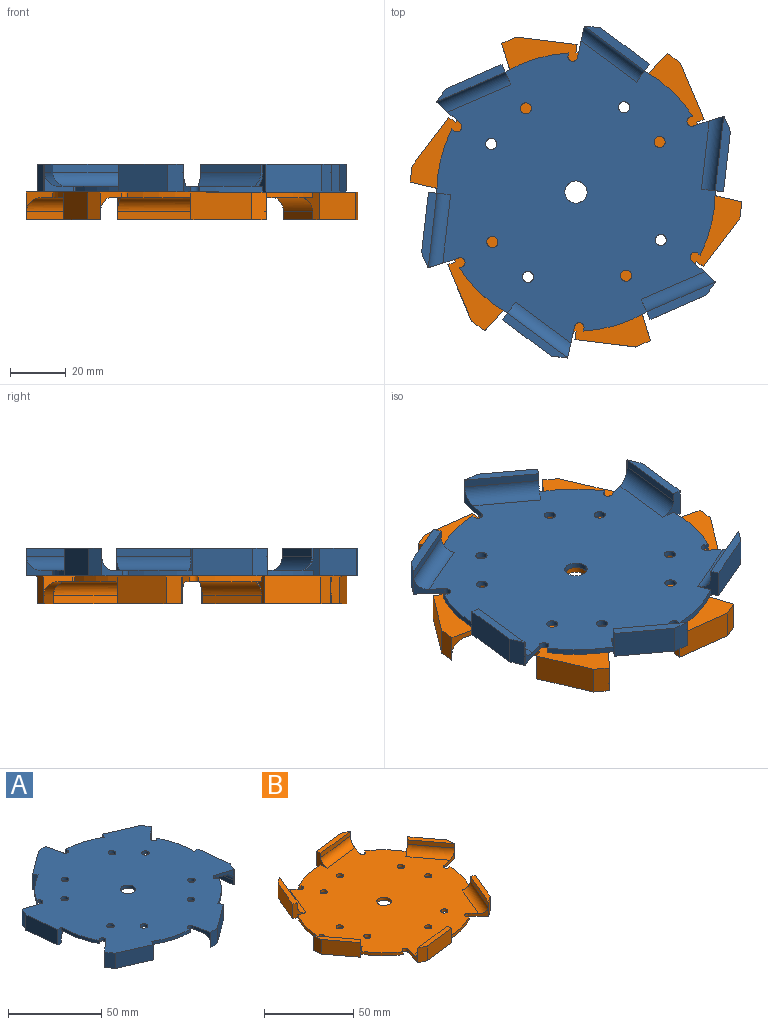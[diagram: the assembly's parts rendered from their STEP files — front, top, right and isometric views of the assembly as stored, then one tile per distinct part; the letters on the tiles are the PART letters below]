
ASSEMBLY  parts=2 mates=1
PART A: 77 faces, bbox 110.9x119.2x10 mm
  f0: cylinder r=50mm len=23.13mm, axis (0,0,1), area 48mm2, adj f1,f33,f34,f41
  f1: plane 2x0.94mm, normal (0.68,-0.74,0), area 2.5mm2, adj f0,f2,f33,f34
  f2: cylinder r=1.76mm len=3.33mm, axis (0,0,1), area 11.2mm2, adj f1,f3,f33,f34
  f3: plane 8.09x7.44mm, normal (-0.68,0.74,0), area 27.9mm2, adj f2,f33,f34,f46,f69
  f4: cylinder r=50mm len=22.76mm, axis (0,0,1), area 48mm2, adj f5,f33,f34,f48
  f5: plane 2x1.24mm, normal (0.98,0.22,0), area 2.5mm2, adj f4,f6,f33,f34
  f6: cylinder r=1.76mm len=3.51mm, axis (0,0,1), area 11.2mm2, adj f5,f7,f33,f34
  f7: plane 10.73x7mm, normal (-0.98,-0.22,0), area 27.9mm2, adj f6,f33,f34,f51,f68
  f8: cylinder r=50mm len=17.31mm, axis (0,0,1), area 48mm2, adj f9,f33,f34,f53
  f9: plane 2x1.21mm, normal (0.3,0.95,0), area 2.5mm2, adj f8,f10,f33,f34
  f10: cylinder r=1.76mm len=3.28mm, axis (0,0,1), area 11.2mm2, adj f9,f11,f33,f34
  f11: plane 10.49x7mm, normal (-0.3,-0.95,0), area 27.9mm2, adj f10,f33,f34,f56,f67
  f12: cylinder r=50mm len=23.13mm, axis (0,0,1), area 48mm2, adj f13,f33,f34,f58
  f13: plane 2x0.94mm, normal (-0.68,0.74,0), area 2.5mm2, adj f12,f14,f33,f34
  f14: cylinder r=1.76mm len=3.33mm, axis (0,0,1), area 11.2mm2, adj f13,f15,f33,f34
  f15: plane 8.09x7.44mm, normal (0.68,-0.74,0), area 27.9mm2, adj f14,f33,f34,f61,f66
  f16: cylinder r=50mm len=22.76mm, axis (0,0,1), area 48mm2, adj f17,f33,f34,f63
  f17: plane 2x1.24mm, normal (-0.98,-0.22,0), area 2.5mm2, adj f16,f18,f33,f34
  f18: cylinder r=1.76mm len=3.51mm, axis (0,0,1), area 11.2mm2, adj f17,f19,f33,f34
  f19: plane 10.73x7mm, normal (0.98,0.22,0), area 27.9mm2, adj f18,f33,f34,f37,f65
  f20: cylinder r=50mm len=17.31mm, axis (0,0,1), area 48mm2, adj f21,f33,f34,f36
  f21: plane 2x1.21mm, normal (-0.3,-0.95,0), area 2.5mm2, adj f20,f22,f33,f34
  f22: cylinder r=1.76mm len=3.28mm, axis (0,0,1), area 11.2mm2, adj f21,f31,f33,f34
  f23: cylinder r=2mm len=4mm, axis (0,0,1), area 25.1mm2, adj f33,f34
  f24: cylinder r=2mm len=4mm, axis (0,0,1), area 25.1mm2, adj f33,f34
  f25: cylinder r=2mm len=4mm, axis (0,0,1), area 25.1mm2, adj f33,f34
  f26: cylinder r=2mm len=4mm, axis (0,0,1), area 25.1mm2, adj f33,f34
  f27: cylinder r=2mm len=4mm, axis (0,0,1), area 25.1mm2, adj f33,f34
  f28: cylinder r=2mm len=4mm, axis (0,0,1), area 25.1mm2, adj f33,f34
  f29: cylinder r=2mm len=4mm, axis (0,0,1), area 25.1mm2, adj f33,f34
  f30: cylinder r=2mm len=4mm, axis (0,0,1), area 25.1mm2, adj f33,f34
  f31: plane 10.49x7mm, normal (0.3,0.95,0), area 27.9mm2, adj f22,f33,f34,f42,f70
  f32: cylinder r=4mm len=8mm, axis (0,0,1), area 50.3mm2, adj f33,f34
  f33: plane 108.35x100mm, normal (0,0,-1), area 7441mm2, adj f0,f1,f2,f3,f4,f5,f6,f7
  f34: plane 119.2x110.91mm, normal (0,0,1), area 8655mm2, adj f0,f1,f2,f3,f4,f5,f6,f7
  f35: plane 21.61x15.99mm, normal (0.59,-0.8,0), area 80.7mm2, adj f36,f37,f39,f65
  f36: plane 10x6.43mm, normal (-0.8,-0.59,0), area 35.4mm2, adj f20,f33,f34,f35,f38,f39,f65
  f37: plane 10x0.09mm, normal (0.8,0.59,0), area 1.1mm2, adj f19,f34,f35,f39,f73
  f38: plane 17.59x13.02mm, normal (-0.59,0.8,0), area 218.9mm2, adj f34,f36,f39,f73
  f39: plane 23.4x16.08mm, normal (0,0,-1), area 73.4mm2, adj f35,f36,f37,f38,f73
  f40: plane 26.71x3.04mm, normal (0.99,0.11,0), area 80.7mm2, adj f41,f42,f44,f70
  f41: plane 10x7.95mm, normal (0.11,-0.99,0), area 35.4mm2, adj f0,f33,f34,f40,f43,f44,f70
  f42: plane 10x0.11mm, normal (-0.11,0.99,0), area 1.1mm2, adj f31,f34,f40,f44,f74
  f43: plane 21.75x10mm, normal (-0.99,-0.11,0), area 218.9mm2, adj f34,f41,f44,f74
  f44: plane 27.05x5.46mm, normal (0,0,-1), area 73.4mm2, adj f40,f41,f42,f43,f74
  f45: plane 24.66x10.72mm, normal (0.4,0.92,0), area 80.7mm2, adj f46,f48,f49,f69
  f46: plane 10x0.1mm, normal (-0.92,0.4,0), area 1.1mm2, adj f3,f34,f45,f49,f75
  f47: plane 20.07x10mm, normal (-0.4,-0.92,0), area 218.9mm2, adj f34,f48,f49,f75
  f48: plane 10x7.34mm, normal (0.92,-0.4,0), area 35.4mm2, adj f4,f33,f34,f45,f47,f49,f69
  f49: plane 24.7x13.47mm, normal (0,0,-1), area 73.4mm2, adj f45,f46,f47,f48,f75
  f50: plane 21.61x15.99mm, normal (-0.59,0.8,0), area 80.7mm2, adj f51,f53,f54,f68
  f51: plane 10x0.09mm, normal (-0.8,-0.59,0), area 1.1mm2, adj f7,f34,f50,f54,f76
  f52: plane 17.59x13.02mm, normal (0.59,-0.8,0), area 218.9mm2, adj f34,f53,f54,f76
  f53: plane 10x6.43mm, normal (0.8,0.59,0), area 35.4mm2, adj f8,f33,f34,f50,f52,f54,f68
  f54: plane 23.4x16.08mm, normal (0,0,-1), area 73.4mm2, adj f50,f51,f52,f53,f76
  f55: plane 26.71x3.04mm, normal (-0.99,-0.11,0), area 80.7mm2, adj f56,f58,f59,f67
  f56: plane 10x0.11mm, normal (0.11,-0.99,0), area 1.1mm2, adj f11,f34,f55,f59,f71
  f57: plane 21.75x10mm, normal (0.99,0.11,0), area 218.9mm2, adj f34,f58,f59,f71
  f58: plane 10x7.95mm, normal (-0.11,0.99,0), area 35.4mm2, adj f12,f33,f34,f55,f57,f59,f67
  f59: plane 27.05x5.46mm, normal (0,0,-1), area 73.4mm2, adj f55,f56,f57,f58,f71
  f60: plane 24.66x10.72mm, normal (-0.4,-0.92,0), area 80.7mm2, adj f61,f63,f64,f66
  f61: plane 10x0.1mm, normal (0.92,-0.4,0), area 1.1mm2, adj f15,f34,f60,f64,f72
  f62: plane 20.07x10mm, normal (0.4,0.92,0), area 218.9mm2, adj f34,f63,f64,f72
  f63: plane 10x7.34mm, normal (-0.92,0.4,0), area 35.4mm2, adj f16,f33,f34,f60,f62,f64,f66
  f64: plane 24.7x13.47mm, normal (0,0,-1), area 73.4mm2, adj f60,f61,f62,f63,f72
  f65: cylinder r=5mm len=24.59mm, axis (0.8,0.59,0), area 204.8mm2, adj f19,f33,f35,f36
  f66: cylinder r=5mm len=26.65mm, axis (0.92,-0.4,0), area 204.8mm2, adj f15,f33,f60,f63
  f67: cylinder r=5mm len=27.28mm, axis (0.11,-0.99,0), area 204.8mm2, adj f11,f33,f55,f58
  f68: cylinder r=5mm len=24.59mm, axis (-0.8,-0.59,0), area 204.8mm2, adj f7,f33,f50,f53
  f69: cylinder r=5mm len=26.65mm, axis (-0.92,0.4,0), area 204.8mm2, adj f3,f33,f45,f48
  f70: cylinder r=5mm len=27.28mm, axis (-0.11,0.99,0), area 204.8mm2, adj f31,f33,f40,f41
  f71: plane 10x5.29mm, normal (0.92,-0.4,0), area 57.7mm2, adj f34,f56,f57,f59
  f72: plane 10x4.64mm, normal (0.8,0.59,0), area 57.7mm2, adj f34,f61,f62,f64
  f73: plane 10x5.74mm, normal (-0.11,0.99,0), area 57.7mm2, adj f34,f37,f38,f39
  f74: plane 10x5.29mm, normal (-0.92,0.4,0), area 57.7mm2, adj f34,f42,f43,f44
  f75: plane 10x4.64mm, normal (-0.8,-0.59,0), area 57.7mm2, adj f34,f46,f47,f49
  f76: plane 10x5.74mm, normal (0.11,-0.99,0), area 57.7mm2, adj f34,f51,f52,f54
PART B: 77 faces, bbox 119.1x111.3x10 mm
  f0: cylinder r=50mm len=22.81mm, axis (0,0,-1), area 48mm2, adj f1,f33,f34,f41
  f1: plane 2x1.24mm, normal (0.23,-0.97,0), area 2.5mm2, adj f0,f2,f33,f34
  f2: cylinder r=1.76mm len=3.51mm, axis (0,0,-1), area 11.2mm2, adj f1,f3,f33,f34
  f3: plane 10.71x7mm, normal (-0.23,0.97,0), area 27.9mm2, adj f2,f33,f34,f46,f69
  f4: cylinder r=50mm len=17.17mm, axis (0,0,-1), area 48mm2, adj f5,f33,f34,f48
  f5: plane 2x1.22mm, normal (0.96,-0.29,0), area 2.5mm2, adj f4,f6,f33,f34
  f6: cylinder r=1.76mm len=3.29mm, axis (0,0,-1), area 11.2mm2, adj f5,f7,f33,f34
  f7: plane 10.52x7mm, normal (-0.96,0.29,0), area 27.9mm2, adj f6,f33,f34,f51,f68
  f8: cylinder r=50mm len=23.08mm, axis (0,0,-1), area 48mm2, adj f9,f33,f34,f53
  f9: plane 2x0.93mm, normal (0.73,0.68,0), area 2.5mm2, adj f8,f10,f33,f34
  f10: cylinder r=1.76mm len=3.32mm, axis (0,0,-1), area 11.2mm2, adj f9,f11,f33,f34
  f11: plane 8.03x7.51mm, normal (-0.73,-0.68,0), area 27.9mm2, adj f10,f33,f34,f56,f67
  f12: cylinder r=50mm len=22.81mm, axis (0,0,-1), area 48mm2, adj f13,f33,f34,f58
  f13: plane 2x1.24mm, normal (-0.23,0.97,0), area 2.5mm2, adj f12,f14,f33,f34
  f14: cylinder r=1.76mm len=3.51mm, axis (0,0,-1), area 11.2mm2, adj f13,f15,f33,f34
  f15: plane 10.71x7mm, normal (0.23,-0.97,0), area 27.9mm2, adj f14,f33,f34,f61,f66
  f16: cylinder r=50mm len=17.17mm, axis (0,0,-1), area 48mm2, adj f17,f33,f34,f63
  f17: plane 2x1.22mm, normal (-0.96,0.29,0), area 2.5mm2, adj f16,f18,f33,f34
  f18: cylinder r=1.76mm len=3.29mm, axis (0,0,-1), area 11.2mm2, adj f17,f19,f33,f34
  f19: plane 10.52x7mm, normal (0.96,-0.29,0), area 27.9mm2, adj f18,f33,f34,f37,f65
  f20: cylinder r=50mm len=23.08mm, axis (0,0,-1), area 48mm2, adj f21,f33,f34,f36
  f21: plane 2x0.93mm, normal (-0.73,-0.68,0), area 2.5mm2, adj f20,f22,f33,f34
  f22: cylinder r=1.76mm len=3.32mm, axis (0,0,-1), area 11.2mm2, adj f21,f31,f33,f34
  f23: cylinder r=2mm len=4mm, axis (0,0,-1), area 25.1mm2, adj f33,f34
  f24: cylinder r=2mm len=4mm, axis (0,0,-1), area 25.1mm2, adj f33,f34
  f25: cylinder r=2mm len=4mm, axis (0,0,-1), area 25.1mm2, adj f33,f34
  f26: cylinder r=2mm len=4mm, axis (0,0,-1), area 25.1mm2, adj f33,f34
  f27: cylinder r=2mm len=4mm, axis (0,0,-1), area 25.1mm2, adj f33,f34
  f28: cylinder r=2mm len=4mm, axis (0,0,-1), area 25.1mm2, adj f33,f34
  f29: cylinder r=2mm len=4mm, axis (0,0,-1), area 25.1mm2, adj f33,f34
  f30: cylinder r=2mm len=4mm, axis (0,0,-1), area 25.1mm2, adj f33,f34
  f31: plane 8.03x7.51mm, normal (0.73,0.68,0), area 27.9mm2, adj f22,f33,f34,f42,f70
  f32: cylinder r=4mm len=8mm, axis (0,0,-1), area 50.3mm2, adj f33,f34
  f33: plane 108.31x100mm, normal (0,0,1), area 7441mm2, adj f0,f1,f2,f3,f4,f5,f6,f7
  f34: plane 119.15x111.29mm, normal (0,0,-1), area 8655mm2, adj f0,f1,f2,f3,f4,f5,f6,f7
  f35: plane 26.69x3.28mm, normal (0.12,-0.99,0), area 80.7mm2, adj f36,f37,f39,f65
  f36: plane 10x7.94mm, normal (-0.99,-0.12,0), area 35.4mm2, adj f20,f33,f34,f35,f38,f39,f65
  f37: plane 10x0.11mm, normal (0.99,0.12,0), area 1.1mm2, adj f19,f34,f35,f39,f73
  f38: plane 21.72x10mm, normal (-0.12,0.99,0), area 218.9mm2, adj f34,f36,f39,f73
  f39: plane 27.05x5.65mm, normal (0,0,1), area 73.4mm2, adj f35,f36,f37,f38,f73
  f40: plane 24.75x10.51mm, normal (0.92,-0.39,0), area 80.7mm2, adj f41,f42,f44,f70
  f41: plane 10x7.36mm, normal (-0.39,-0.92,0), area 35.4mm2, adj f0,f33,f34,f40,f43,f44,f70
  f42: plane 10x0.1mm, normal (0.39,0.92,0), area 1.1mm2, adj f31,f34,f40,f44,f74
  f43: plane 20.15x10mm, normal (-0.92,0.39,0), area 218.9mm2, adj f34,f41,f44,f74
  f44: plane 24.79x13.27mm, normal (0,0,1), area 73.4mm2, adj f40,f41,f42,f43,f74
  f45: plane 21.47x16.18mm, normal (0.8,0.6,0), area 80.7mm2, adj f46,f48,f49,f69
  f46: plane 10x0.09mm, normal (-0.6,0.8,0), area 1.1mm2, adj f3,f34,f45,f49,f75
  f47: plane 17.48x13.17mm, normal (-0.8,-0.6,0), area 218.9mm2, adj f34,f48,f49,f75
  f48: plane 10x6.39mm, normal (0.6,-0.8,0), area 35.4mm2, adj f4,f33,f34,f45,f47,f49,f69
  f49: plane 23.28x16.27mm, normal (0,0,1), area 73.4mm2, adj f45,f46,f47,f48,f75
  f50: plane 26.69x3.28mm, normal (-0.12,0.99,0), area 80.7mm2, adj f51,f53,f54,f68
  f51: plane 10x0.11mm, normal (-0.99,-0.12,0), area 1.1mm2, adj f7,f34,f50,f54,f76
  f52: plane 21.72x10mm, normal (0.12,-0.99,0), area 218.9mm2, adj f34,f53,f54,f76
  f53: plane 10x7.94mm, normal (0.99,0.12,0), area 35.4mm2, adj f8,f33,f34,f50,f52,f54,f68
  f54: plane 27.05x5.65mm, normal (0,0,1), area 73.4mm2, adj f50,f51,f52,f53,f76
  f55: plane 24.75x10.51mm, normal (-0.92,0.39,0), area 80.7mm2, adj f56,f58,f59,f67
  f56: plane 10x0.1mm, normal (-0.39,-0.92,0), area 1.1mm2, adj f11,f34,f55,f59,f71
  f57: plane 20.15x10mm, normal (0.92,-0.39,0), area 218.9mm2, adj f34,f58,f59,f71
  f58: plane 10x7.36mm, normal (0.39,0.92,0), area 35.4mm2, adj f12,f33,f34,f55,f57,f59,f67
  f59: plane 24.79x13.27mm, normal (0,0,1), area 73.4mm2, adj f55,f56,f57,f58,f71
  f60: plane 21.47x16.18mm, normal (-0.8,-0.6,0), area 80.7mm2, adj f61,f63,f64,f66
  f61: plane 10x0.09mm, normal (0.6,-0.8,0), area 1.1mm2, adj f15,f34,f60,f64,f72
  f62: plane 17.48x13.17mm, normal (0.8,0.6,0), area 218.9mm2, adj f34,f63,f64,f72
  f63: plane 10x6.39mm, normal (-0.6,0.8,0), area 35.4mm2, adj f16,f33,f34,f60,f62,f64,f66
  f64: plane 23.28x16.27mm, normal (0,0,1), area 73.4mm2, adj f60,f61,f62,f63,f72
  f65: cylinder r=5mm len=27.3mm, axis (0.99,0.12,0), area 204.8mm2, adj f19,f33,f35,f36
  f66: cylinder r=5mm len=24.48mm, axis (0.6,-0.8,0), area 204.8mm2, adj f15,f33,f60,f63
  f67: cylinder r=5mm len=26.7mm, axis (-0.39,-0.92,0), area 204.8mm2, adj f11,f33,f55,f58
  f68: cylinder r=5mm len=27.3mm, axis (-0.99,-0.12,0), area 204.8mm2, adj f7,f33,f50,f53
  f69: cylinder r=5mm len=24.48mm, axis (-0.6,0.8,0), area 204.8mm2, adj f3,f33,f45,f48
  f70: cylinder r=5mm len=26.7mm, axis (0.39,0.92,0), area 204.8mm2, adj f31,f33,f40,f41
  f71: plane 10x4.61mm, normal (0.6,-0.8,0), area 57.7mm2, adj f34,f56,f57,f59
  f72: plane 10x5.73mm, normal (0.99,0.12,0), area 57.7mm2, adj f34,f61,f62,f64
  f73: plane 10x5.31mm, normal (0.39,0.92,0), area 57.7mm2, adj f34,f37,f38,f39
  f74: plane 10x4.61mm, normal (-0.6,0.8,0), area 57.7mm2, adj f34,f42,f43,f44
  f75: plane 10x5.73mm, normal (-0.99,-0.12,0), area 57.7mm2, adj f34,f46,f47,f49
  f76: plane 10x5.31mm, normal (-0.39,-0.92,0), area 57.7mm2, adj f34,f51,f52,f54
PLACE A rot(axis=(0,-1,0),180deg) t=(265.24,42.53,-80.16)mm
PLACE B rot(axis=(1,0,0),180deg) t=(265.24,42.53,-80.16)mm
MATE pin_slot B.f32 <-> A.f32  axis (0,0,1) through (265.24,42.53,-80.16)mm
